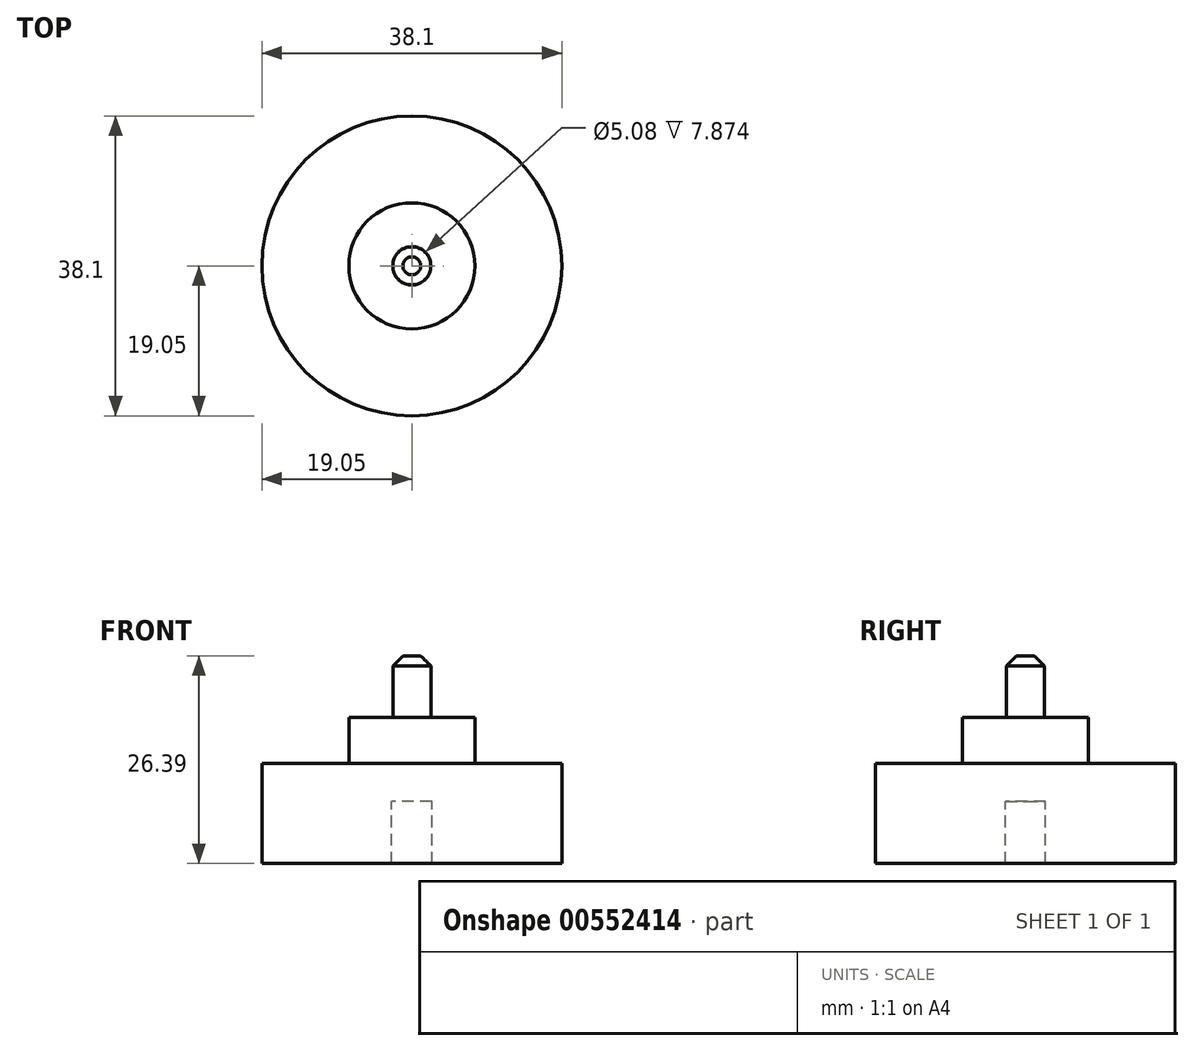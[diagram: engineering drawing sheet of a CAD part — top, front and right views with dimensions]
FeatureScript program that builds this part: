
annotation { "Feature Type Name" : "Feature", "Feature Type Description" : "" }
export const myFeature = defineFeature(function(context is Context, id is Id, definition is map)
    precondition{}
    {
        {
            var Q0;
            Q0=qCreatedBy(makeId("Front.planeOp"),FACE);
            var sketch = newSketch(context, id + "F0", { "sketchPlane" : qUnion([Q0])});
            skLineSegment(sketch, "E0", {"start": v(19.05, 0) * mm, "end": v(19.05, 12.7) * mm});
            skLineSegment(sketch, "E1", {"start": v(19.05, 12.7) * mm, "end": v(8, 12.7) * mm});
            skLineSegment(sketch, "E2", {"start": v(2.41, 18.54) * mm, "end": v(8, 18.54) * mm});
            skLineSegment(sketch, "E3", {"start": v(8, 18.54) * mm, "end": v(8, 12.7) * mm});
            skLineSegment(sketch, "E4", {"start": v(0, 26.4) * mm, "end": v(2.41, 26.4) * mm});
            skLineSegment(sketch, "E5", {"start": v(2.41, 26.4) * mm, "end": v(2.41, 18.54) * mm});
            skPoint(sketch, "E5.endSnap0", {"position": v(0, 15.62) * mm});
            skPoint(sketch, "E6.orphan", {"position": v(2.41, 15.62) * mm});
            skPoint(sketch, "E7.orphan", {"position": v(0, 12.7) * mm});
            skPoint(sketch, "E8.start.orphan", {"position": v(0, 18.54) * mm});
            skLineSegment(sketch, "E9", {"start": v(2.54, 0) * mm, "end": v(2.54, 7.87) * mm});
            skLineSegment(sketch, "E10", {"start": v(2.54, 7.87) * mm, "end": v(0, 7.87) * mm});
            skLineSegment(sketch, "E11", {"start": v(0, 26.4) * mm, "end": v(0, 7.87) * mm});
            skLineSegment(sketch, "E12", {"start": v(19.05, 0) * mm, "end": v(2.54, 0) * mm});
            skSolve(sketch);
        }
        {
            var Q0;
            Q0 = qSketchRegion(id + "F0", true);
            var Q1;
            Q1=sQuery(id+"F0.wireOp",EDGE,"E11");
            revolve(context, id + "F1", {"entities" : qUnion([Q0]), "axis" : qUnion([Q1]), "revolveType" : RevolveType.FULL});
        }
        {
            var Q0;
            Q0=makeQuery(id+"F1.opRevolve","SWEPT_EDGE",EDGE,{"disambiguationData":[OSD([sQuery(id+"F0.wireOp",EDGE,"E4"),sQuery(id+"F0.wireOp",EDGE,"E5")])]});
            chamfer(context, id + "F2", {"entities" : qUnion([Q0]), "width" : 1.27 * mm, "tangentPropagation" : true});
        }
    });
